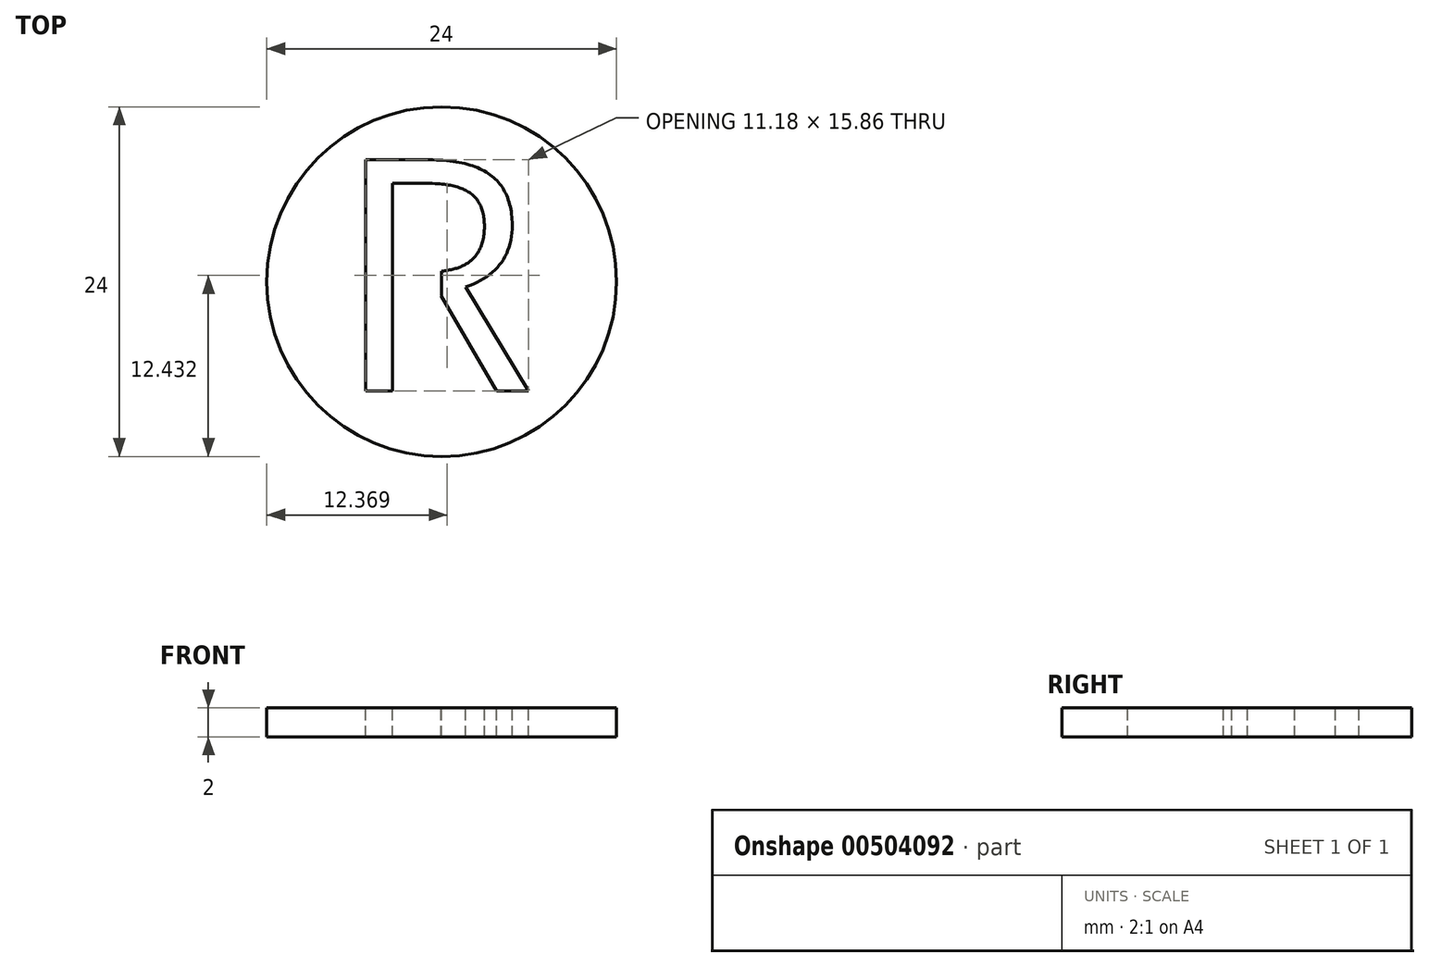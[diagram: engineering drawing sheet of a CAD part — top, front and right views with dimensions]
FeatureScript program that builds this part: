
annotation { "Feature Type Name" : "Feature", "Feature Type Description" : "" }
export const myFeature = defineFeature(function(context is Context, id is Id, definition is map)
    precondition{}
    {
        {
            var Q0;
            Q0=qCreatedBy(makeId("Top.planeOp"),FACE);
            var sketch = newSketch(context, id + "F0", { "sketchPlane" : qUnion([Q0])});
            skCircle(sketch, "E0", {"center": v(0, 0) * mm, "radius": 12 * mm});
            skSolve(sketch);
        }
        {
            var Q0;
            Q0=qSketchRegion(id+"F0",true);
            extrude(context, id + "F1", {"entities" : qUnion([Q0]), "depth" : 2 * mm});
        }
        {
            var Q0;
            Q0=makeQuery(id+"F1.opExtrude","CAP_FACE",FACE,{"disambiguationData":[OSD([sQuery(id+"F0.wireOp",EDGE,"E0")])],"isStart":false});
            var sketch = newSketch(context, id + "F2", { "sketchPlane" : qUnion([Q0])});
            skPoint(sketch, "E1", {"position": v(0, 12) * mm});
            skText(sketch, "E2", { "text": "R", "fontName": "OpenSans-Regular.ttf"});
            skPoint(sketch, "E3", {"position": v(0, 9) * mm});
            skLineSegment(sketch, "E4.bottom", {"start": v(-3.4, 3.94) * mm, "end": v(0, 3.94) * mm});
            skLineSegment(sketch, "E4.top", {"start": v(-3.4, -0.95) * mm, "end": v(0, -0.95) * mm});
            skLineSegment(sketch, "E4.left", {"start": v(-3.4, 3.94) * mm, "end": v(-3.4, -0.95) * mm});
            skLineSegment(sketch, "E4.right", {"start": v(0, 3.94) * mm, "end": v(0, -0.95) * mm});
            const initialGuessF2  = {"E2": [-0.0074, -0.0075, 1, 0, 0.016]};
            skSetInitialGuess(sketch, initialGuessF2);
            skSolve(sketch);
        }
        {
            var Q0;
            {var subQ6=sQuery(id+"F2.wireOp",EDGE,"E2.sketch_text.stroke-1");Q0=makeQuery(id+"F2.imprint","IMPRINT",FACE,{"disambiguationData":[TD([[makeQuery(id+"F2.imprint","IMPRINT",EDGE,{"derivedFrom":subQ6}),-1.0]])]});}
            extrude(context, id + "F3", {"entities" : qUnion([Q0]), "operationType" : NewBodyOperationType.REMOVE, "oppositeDirection" : true, "depth" : 25 * mm});
        }
    });
